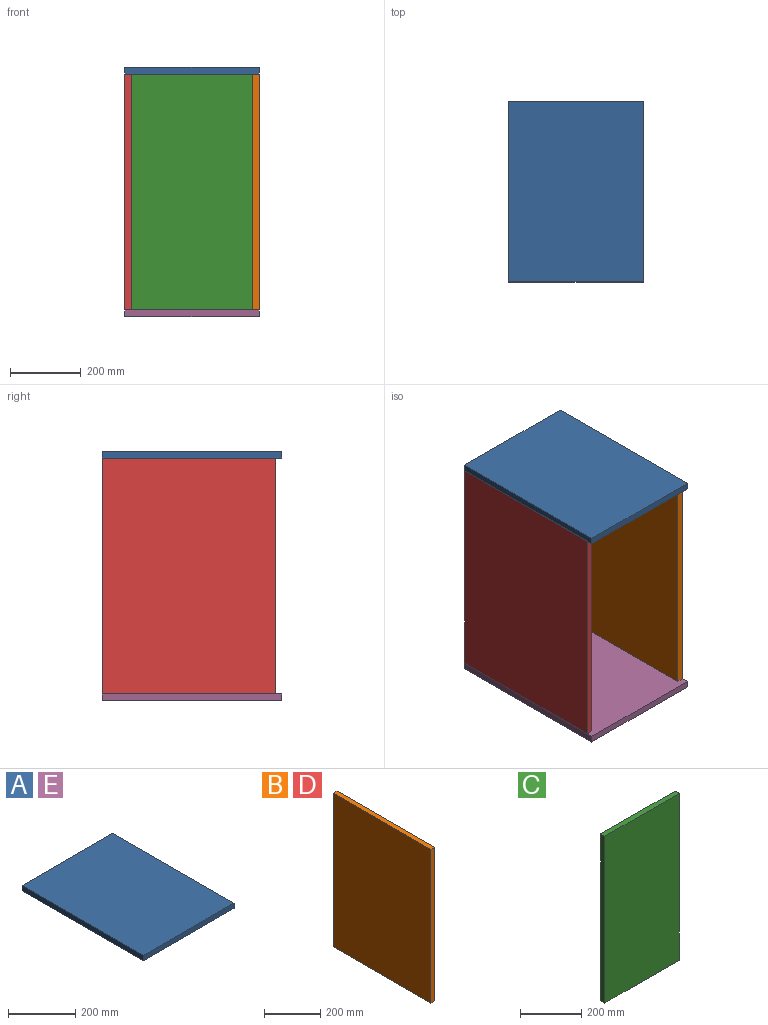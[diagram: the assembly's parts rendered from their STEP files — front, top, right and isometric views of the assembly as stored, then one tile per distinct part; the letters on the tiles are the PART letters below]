
ASSEMBLY  parts=5 mates=2
PART A: 6 faces, bbox 381x508x19.1 mm
  f0: plane 381x19.05mm, normal (0,-1,0), area 7258mm2, adj f1,f3,f4,f5
  f1: plane 508x19.05mm, normal (1,0,0), area 9677.4mm2, adj f0,f2,f4,f5
  f2: plane 381x19.05mm, normal (0,1,0), area 7258.1mm2, adj f1,f3,f4,f5
  f3: plane 508x19.05mm, normal (-1,0,0), area 9677.4mm2, adj f0,f2,f4,f5
  f4: plane 508x381mm, normal (0,0,1), area 193548mm2, adj f0,f1,f2,f3
  f5: plane 508x381mm, normal (0,0,-1), area 193548mm2, adj f0,f1,f2,f3
PART B: 6 faces, bbox 19.1x489x666.8 mm
  f0: plane 666.75x19.05mm, normal (0,1,0), area 12701.6mm2, adj f1,f3,f4,f5
  f1: plane 666.75x488.95mm, normal (-1,0,0), area 326007.4mm2, adj f0,f2,f4,f5
  f2: plane 666.75x19.05mm, normal (0,-1,0), area 12701.6mm2, adj f1,f3,f4,f5
  f3: plane 666.75x488.95mm, normal (1,0,0), area 326007.4mm2, adj f0,f2,f4,f5
  f4: plane 488.95x19.05mm, normal (0,0,1), area 9314.5mm2, adj f0,f1,f2,f3
  f5: plane 488.95x19.05mm, normal (0,0,-1), area 9314.5mm2, adj f0,f1,f2,f3
PART C: 6 faces, bbox 342.9x19.1x666.8 mm
  f0: plane 342.9x19.05mm, normal (0,0,1), area 6532.2mm2, adj f1,f2,f3,f4
  f1: plane 666.75x19.05mm, normal (-1,0,0), area 12701.6mm2, adj f0,f2,f4,f5
  f2: plane 666.75x342.9mm, normal (0,-1,0), area 228628.6mm2, adj f0,f1,f3,f5
  f3: plane 666.75x19.05mm, normal (1,0,0), area 12701.6mm2, adj f0,f2,f4,f5
  f4: plane 666.75x342.9mm, normal (0,1,0), area 228628.6mm2, adj f0,f1,f3,f5
  f5: plane 342.9x19.05mm, normal (0,0,-1), area 6532.2mm2, adj f1,f2,f3,f4
PART D: same geometry as B
PART E: same geometry as A
PLACE A t=(0,0,685.8)mm
PLACE B at identity
PLACE C at identity fixed
PLACE D t=(-361.95,0,0)mm
PLACE E at identity
MATE fastened A.f5 <-> B.f4  axis (0,0,-1) through (190.5,254,685.8)mm
MATE fastened C.f1 <-> D.f3  axis (-1,0,0) through (-171.45,254,685.8)mm
